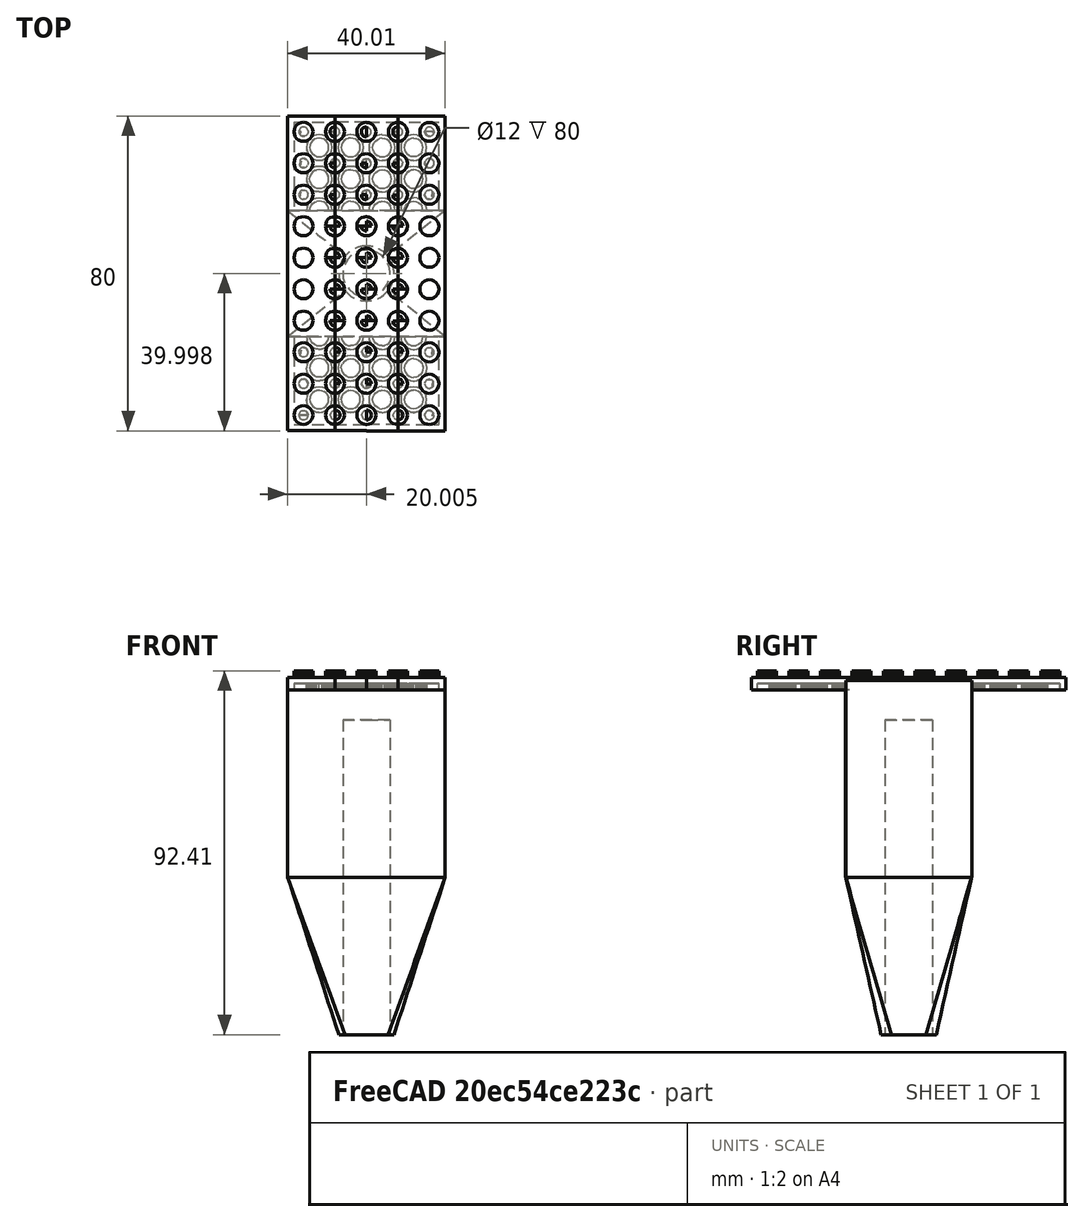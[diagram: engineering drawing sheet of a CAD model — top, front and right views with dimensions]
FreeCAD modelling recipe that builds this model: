
FCSTD DOCUMENT  (FreeCAD 0.20R29177 +426 (Git))
Label: upperShaftHolder
License: All rights reserved
LicenseURL: https://en.wikipedia.org/wiki/All_rights_reserved
objects: Sketcher::SketchObject×4, Part::Feature×3, Part::Refine×3, Part::MultiFuse×1, PartDesign::FeatureBase×1, PartDesign::Pad×1, PartDesign::AdditiveLoft×1, PartDesign::Pocket×1, PartDesign::Body×1
note: 19 computed .brp shape members not serialized (recipe doc carries the construction recipe); baked Part::Feature solids carry a one-line shape summary decoded from their .brp

FEATURE [Part::Feature] Component001001_solid  label="Component001001 (Solid)"
  shape: bbox 12 x 79.98 x 4.799 mm, 9304 faces (baked)
FEATURE [Part::Feature] Component002001_solid  label="Component002001 (Solid)"
  shape: bbox 12 x 79.97 x 4.799 mm, 9128 faces (baked)
FEATURE [Part::Feature] Component002002_solid  label="Component002002 (Solid)"
  shape: bbox 15.99 x 80 x 4.799 mm, 20521 faces (baked)
FEATURE [Part::Refine] Component001001_solid001  label="Component001001 (Solid)001"
  Source = -> Component001001_solid
FEATURE [Part::Refine] Component002001_solid001  label="Component002001 (Solid)001"
  Source = -> Component002001_solid
FEATURE [Part::Refine] Component002002_solid001  label="Component002002 (Solid)001"
  Source = -> Component002002_solid
FEATURE [Part::MultiFuse] Fusion
  Refine = true
  Shapes = -> [Component001001_solid001,Component002001_solid001,Component002002_solid001]
FEATURE [PartDesign::FeatureBase] BaseFeature
  BaseFeature = -> Fusion
FEATURE [Sketcher::SketchObject] Sketch
  FullyConstrained = true
  MapMode = 45
  Placement = pos=(-17.9948,-40.0015,2.38772) rot=(-3.8e-05,-0.002789,0.999996;0.000317rad)
  Support = -> [BaseFeature]
  sketch-geometry (4):
    g0: LineSegment StartX=-20 StartY=16 StartZ=0 EndX=20 EndY=16 EndZ=0
    g1: LineSegment StartX=20 StartY=16 StartZ=0 EndX=20 EndY=-16 EndZ=0
    g2: LineSegment StartX=20 StartY=-16 StartZ=0 EndX=-20 EndY=-16 EndZ=0
    g3: LineSegment StartX=-20 StartY=-16 StartZ=0 EndX=-20 EndY=16 EndZ=0
  constraints (10):
    c: Coincident(g0,g1)
    c: Coincident(g1,g2)
    c: Coincident(g2,g3)
    c: Coincident(g3,g0)
    c: Horizontal(g2)
    c: Vertical(g3)
    c: DistanceX(g0,g0) = 40
    c: DistanceY(g1,g1) = 32
    c: Symmetric(g0,g1,g-1)
    c: Symmetric(g0,g0,g-2)
FEATURE [PartDesign::Pad] Pad
  BaseFeature = -> BaseFeature
  Direction = (-8.85246e-07,1.18241e-08,1)
  Length = 50
  Length2 = 10
  Profile = -> Sketch
  ReferenceAxis = -> Sketch [N_Axis]
  Refine = true
  Reversed = true
  Type = 0
FEATURE [Sketcher::SketchObject] Sketch001
  FullyConstrained = true
  MapMode = 45
  Placement = pos=(-17.9948,-40.0015,-47.6123) rot=(0,0,1;1.57111rad)
  Support = -> [Pad]
  sketch-geometry (5):
    g0: LineSegment StartX=16 StartY=20 StartZ=0 EndX=16 EndY=-20 EndZ=0
    g1: LineSegment StartX=16 StartY=-20 StartZ=0 EndX=-16 EndY=-20 EndZ=0
    g2: LineSegment StartX=-16 StartY=-20 StartZ=0 EndX=-16 EndY=20 EndZ=0
    g3: LineSegment StartX=-16 StartY=20 StartZ=0 EndX=16 EndY=20 EndZ=0
    g4: GeomPoint X=0 Y=0 Z=0
  constraints (12):
    c: Coincident(g0,g1)
    c: Coincident(g1,g2)
    c: Coincident(g2,g3)
    c: Coincident(g3,g0)
    c: Horizontal(g1)
    c: Horizontal(g3)
    c: Vertical(g0)
    c: Vertical(g2)
    c: Symmetric(g1,g0,g4)
    c: Coincident(g4,g-1)
    c: DistanceX(g1,g4) = 16
    c: DistanceY(g4,g0) = 20
FEATURE [Sketcher::SketchObject] Sketch004
  AttachmentOffset = pos=(0,0,-40) rot=(0,0,1;0rad)
  FullyConstrained = true
  MapMode = 45
  Placement = pos=(-17.9947,-40.0015,-87.6123) rot=(0,0,1;1.57111rad)
  Support = -> [Pad]
  sketch-geometry (1):
    g0: Circle CenterX=0 CenterY=0 CenterZ=0 NormalX=0 NormalY=0 NormalZ=1 AngleXU=0 Radius=7
  constraints (2):
    c: Coincident(g0,g-1)
    c: Diameter(g0) = 14
FEATURE [PartDesign::AdditiveLoft] AdditiveLoft
  BaseFeature = -> Pad
  Closed = false
  Profile = -> Sketch001
  Refine = true
  Ruled = false
  Sections = -> [Sketch004]
FEATURE [Sketcher::SketchObject] Sketch005
  FullyConstrained = true
  MapMode = 45
  Placement = pos=(-17.9947,-40.0015,-87.6123) rot=(0,0,-1;1.58415rad)
  Support = -> [AdditiveLoft]
  sketch-geometry (1):
    g0: Circle CenterX=0 CenterY=0 CenterZ=0 NormalX=0 NormalY=0 NormalZ=1 AngleXU=0 Radius=6
  constraints (2):
    c: Coincident(g0,g-1)
    c: Diameter(g0) = 12
FEATURE [PartDesign::Pocket] Pocket
  BaseFeature = -> AdditiveLoft
  Direction = (8.85246e-07,-1.18241e-08,-1)
  Length = 80
  Length2 = 5
  Profile = -> Sketch005
  ReferenceAxis = -> Sketch005 [N_Axis]
  Refine = true
  Reversed = true
  Type = 0
FEATURE [PartDesign::Body] Body
  BaseFeature = -> Fusion
  Group = -> [BaseFeature,Sketch,Pad,Sketch001,Sketch004,AdditiveLoft,Sketch005,Pocket]
  Origin = -> Origin
  Tip = -> Pocket
